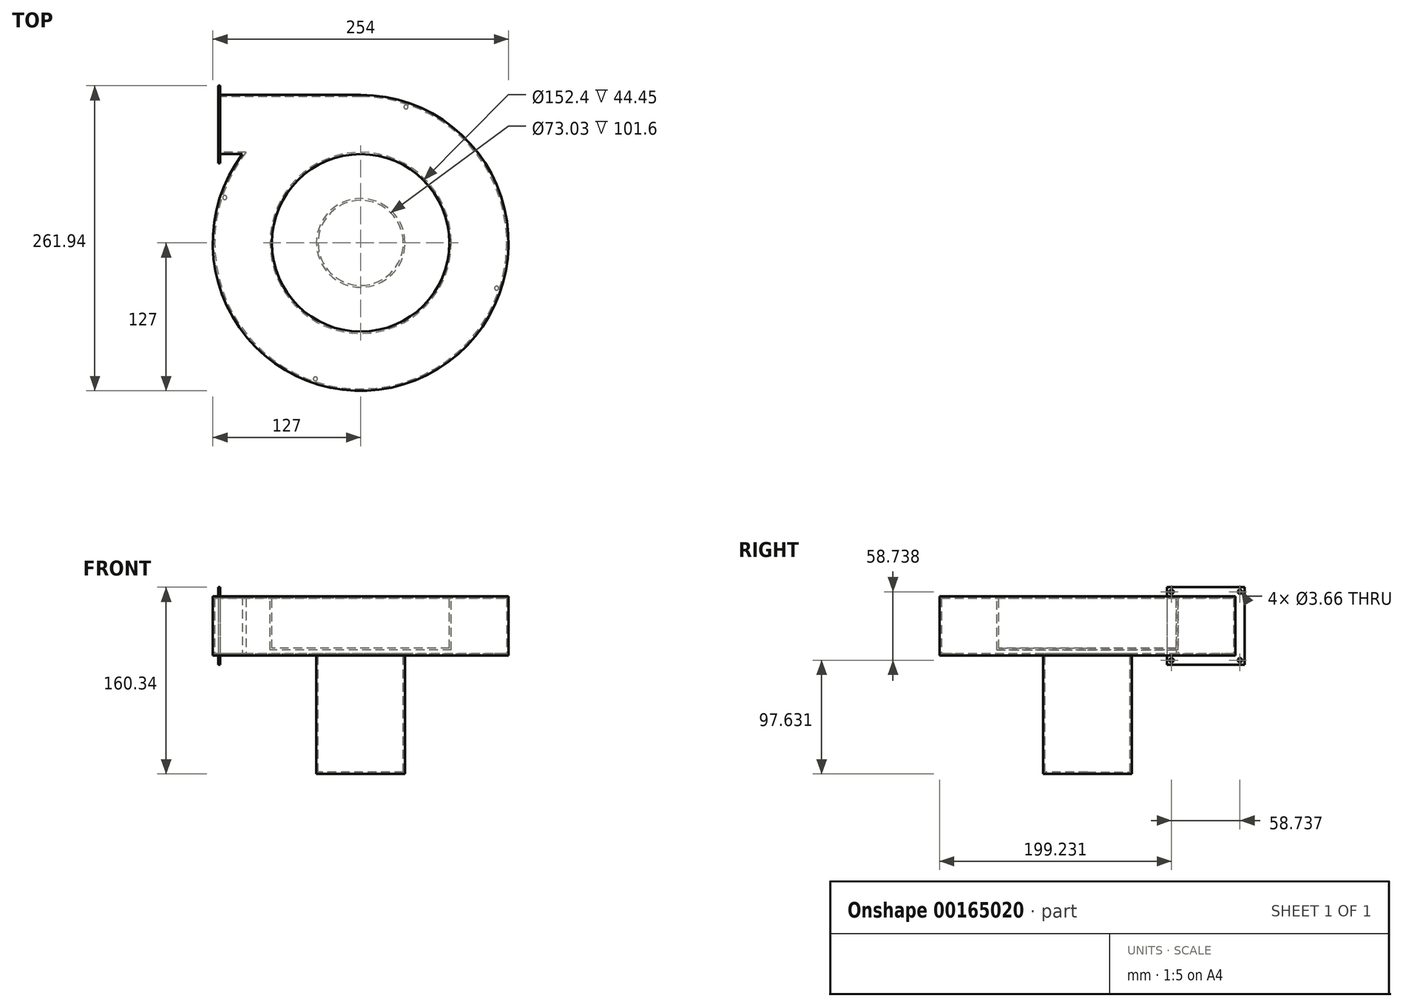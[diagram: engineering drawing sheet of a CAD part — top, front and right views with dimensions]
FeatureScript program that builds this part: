
annotation { "Feature Type Name" : "Feature", "Feature Type Description" : "" }
export const myFeature = defineFeature(function(context is Context, id is Id, definition is map)
    precondition{}
    {
        {
            var Q0;
            Q0=qCreatedBy(makeId("Top.planeOp"),FACE);
            var sketch = newSketch(context, id + "F0", { "sketchPlane" : qUnion([Q0])});
            skLineSegment(sketch, "E0.bottom", {"start": v(-101.6, 76.2) * mm, "end": v(-120.65, 76.2) * mm});
            skLineSegment(sketch, "E0.top", {"start": v(0, 127) * mm, "end": v(-120.65, 127) * mm});
            skLineSegment(sketch, "E1.top", {"start": v(-120.65, 68.26) * mm, "end": v(-122.24, 68.26) * mm});
            skLineSegment(sketch, "E1.left", {"start": v(-120.65, 76.2) * mm, "end": v(-120.65, 68.26) * mm});
            skLineSegment(sketch, "E2.top", {"start": v(-120.65, 134.94) * mm, "end": v(-122.24, 134.94) * mm});
            skLineSegment(sketch, "E2.left", {"start": v(-120.65, 127) * mm, "end": v(-120.65, 134.94) * mm});
            skLineSegment(sketch, "E3", {"start": v(-122.24, 134.94) * mm, "end": v(-122.24, 68.26) * mm});
            skLineSegment(sketch, "E4", {"start": v(-120.65, 76.2) * mm, "end": v(-120.65, 127) * mm, "construction": true});
            skArc(sketch, "E5", {"start": v(-101.6, 76.2) * mm, "mid": v(56.8, -113.6) * mm, "end": v(0, 127) * mm});
            skSolve(sketch);
        }
        {
            var Q0;
            Q0=makeQuery(id+"F0.imprint","IMPRINT",FACE,{"disambiguationData":[TD([[makeQuery(id+"F0.imprint","IMPRINT",EDGE,{"derivedFrom":sQuery(id+"F0.wireOp",EDGE,"E0.bottom")}),-1.0]])]});
            extrude(context, id + "F1", {"entities" : qUnion([Q0]), "depth" : 50.8 * mm});
        }
        {
            var Q0;
            Q0=makeQuery(id+"F1.opExtrude","CAP_FACE",FACE,{"disambiguationData":[OSD([sQuery(id+"F0.wireOp",EDGE,"E0.bottom"),sQuery(id+"F0.wireOp",EDGE,"E0.top"),sQuery(id+"F0.wireOp",EDGE,"E1.top"),sQuery(id+"F0.wireOp",EDGE,"E1.left"),sQuery(id+"F0.wireOp",EDGE,"E2.top"),sQuery(id+"F0.wireOp",EDGE,"E2.left"),sQuery(id+"F0.wireOp",EDGE,"E3"),sQuery(id+"F0.wireOp",EDGE,"E5")])],"isStart":false});
            var sketch = newSketch(context, id + "F2", { "sketchPlane" : qUnion([Q0])});
            skCircle(sketch, "E6", {"center": v(0, 0) * mm, "radius": 76.2 * mm});
            skSolve(sketch);
        }
        {
            var Q0;
            Q0 = qSketchRegion(id + "F2", true);
            extrude(context, id + "F3", {"entities" : qUnion([Q0]), "operationType" : NewBodyOperationType.REMOVE, "oppositeDirection" : true, "depth" : 44.45 * mm});
        }
        {
            var Q0;
            Q0=makeQuery(id+"F1.opExtrude","CAP_FACE",FACE,{"disambiguationData":[OSD([sQuery(id+"F0.wireOp",EDGE,"E0.bottom"),sQuery(id+"F0.wireOp",EDGE,"E0.top"),sQuery(id+"F0.wireOp",EDGE,"E1.top"),sQuery(id+"F0.wireOp",EDGE,"E1.left"),sQuery(id+"F0.wireOp",EDGE,"E2.top"),sQuery(id+"F0.wireOp",EDGE,"E2.left"),sQuery(id+"F0.wireOp",EDGE,"E3"),sQuery(id+"F0.wireOp",EDGE,"E5")])],"isStart":true});
            var sketch = newSketch(context, id + "F4", { "sketchPlane" : qUnion([Q0])});
            skCircle(sketch, "E7", {"center": v(0, 0) * mm, "radius": 38.1 * mm});
            skSolve(sketch);
        }
        {
            var Q0;
            Q0=makeQuery(id+"F4.imprint","IMPRINT",FACE,{"disambiguationData":[TD([[makeQuery(id+"F4.imprint","IMPRINT",EDGE,{"derivedFrom":sQuery(id+"F4.wireOp",EDGE,"E7")}),1.0]])]});
            extrude(context, id + "F5", {"entities" : qUnion([Q0]), "operationType" : NewBodyOperationType.ADD, "depth" : 101.6 * mm});
        }
        {
            var Q0;
            Q0=makeQuery(id+"F1.opExtrude","SWEPT_FACE",FACE,{"disambiguationData":[OSD([sQuery(id+"F0.wireOp",EDGE,"E3")])]});
            shell(context, id + "F6", {"entities" : qUnion([Q0]), "thickness" : 1.59 * mm});
        }
        {
            var Q0;
            Q0=makeQuery(id+"F1.opExtrude","SWEPT_FACE",FACE,{"disambiguationData":[OSD([sQuery(id+"F0.wireOp",EDGE,"E3")])]});
            var sketch = newSketch(context, id + "F7", { "sketchPlane" : qUnion([Q0])});
            skLineSegment(sketch, "E8.bottom", {"start": v(-125.41, 49.21) * mm, "end": v(-77.79, 49.21) * mm});
            skLineSegment(sketch, "E8.top", {"start": v(-125.41, 1.59) * mm, "end": v(-77.79, 1.59) * mm});
            skLineSegment(sketch, "E8.left", {"start": v(-125.41, 49.21) * mm, "end": v(-125.41, 1.59) * mm});
            skLineSegment(sketch, "E8.right", {"start": v(-77.79, 49.21) * mm, "end": v(-77.79, 1.59) * mm});
            skPoint(sketch, "E8.middle", {"position": v(-101.6, 25.4) * mm});
            skLineSegment(sketch, "E9.bottom", {"start": v(-68.26, 58.74) * mm, "end": v(-134.94, 58.74) * mm});
            skLineSegment(sketch, "E9.top", {"start": v(-68.26, -7.94) * mm, "end": v(-134.94, -7.94) * mm});
            skLineSegment(sketch, "E9.left", {"start": v(-68.26, 58.74) * mm, "end": v(-68.26, -7.94) * mm});
            skLineSegment(sketch, "E9.right", {"start": v(-134.94, 58.74) * mm, "end": v(-134.94, -7.94) * mm});
            skSolve(sketch);
        }
        {
            var Q0;
            Q0 = qSketchRegion(id + "F7", true);
            var Q1;
            Q1=makeQuery(id+"F1.opExtrude","SWEPT_FACE",FACE,{"disambiguationData":[OSD([sQuery(id+"F0.wireOp",EDGE,"E2.left")])]});
            extrude(context, id + "F8", {"entities" : qUnion([Q0]), "operationType" : NewBodyOperationType.ADD, "endBound" : BoundingType.UP_TO_SURFACE, "oppositeDirection" : true, "endBoundEntityFace" : qUnion([Q1]), "depth" : 25.4 * mm});
        }
        {
            var Q0;
            Q0=makeQuery(id+"F1.opExtrude","SWEPT_FACE",FACE,{"disambiguationData":[OSD([sQuery(id+"F0.wireOp",EDGE,"E3")])]});
            var sketch = newSketch(context, id + "F9", { "sketchPlane" : qUnion([Q0])});
            skLineSegment(sketch, "E10", {"start": v(-101.6, 49.21) * mm, "end": v(-101.6, 1.59) * mm, "construction": true});
            skLineSegment(sketch, "E11.bottom", {"start": v(-130.97, 58.74) * mm, "end": v(-134.94, 58.74) * mm, "construction": true});
            skLineSegment(sketch, "E11.top", {"start": v(-130.97, 54.77) * mm, "end": v(-134.94, 54.77) * mm, "construction": true});
            skLineSegment(sketch, "E11.left", {"start": v(-130.97, 58.74) * mm, "end": v(-130.97, 54.77) * mm, "construction": true});
            skLineSegment(sketch, "E11.right", {"start": v(-134.94, 58.74) * mm, "end": v(-134.94, 54.77) * mm, "construction": true});
            skLineSegment(sketch, "E12.bottom", {"start": v(-130.97, 54.77) * mm, "end": v(-72.23, 54.77) * mm, "construction": true});
            skLineSegment(sketch, "E12.top", {"start": v(-130.97, -3.97) * mm, "end": v(-72.23, -3.97) * mm, "construction": true});
            skLineSegment(sketch, "E12.left", {"start": v(-130.97, 54.77) * mm, "end": v(-130.97, -3.97) * mm, "construction": true});
            skLineSegment(sketch, "E12.right", {"start": v(-72.23, 54.77) * mm, "end": v(-72.23, -3.97) * mm, "construction": true});
            skPoint(sketch, "E12.middle", {"position": v(-101.6, 25.4) * mm});
            skCircle(sketch, "E13", {"center": v(-130.97, 54.77) * mm, "radius": 1.83 * mm});
            skCircle(sketch, "E14", {"center": v(-72.23, 54.77) * mm, "radius": 1.83 * mm});
            skCircle(sketch, "E15", {"center": v(-72.23, -3.97) * mm, "radius": 1.83 * mm});
            skCircle(sketch, "E16", {"center": v(-130.97, -3.97) * mm, "radius": 1.83 * mm});
            skSolve(sketch);
        }
        {
            var Q0;
            Q0 = qSketchRegion(id + "F9", true);
            var Q1;
            Q1=makeQuery(id+"F1.opExtrude","SWEPT_FACE",FACE,{"disambiguationData":[OSD([sQuery(id+"F0.wireOp",EDGE,"E2.left")])]});
            extrude(context, id + "F10", {"entities" : qUnion([Q0]), "operationType" : NewBodyOperationType.REMOVE, "endBound" : BoundingType.UP_TO_SURFACE, "oppositeDirection" : true, "endBoundEntityFace" : qUnion([Q1]), "depth" : 25.4 * mm});
        }
        {
            var Q0;
            Q0=makeQuery(id+"F1.opExtrude","CAP_FACE",FACE,{"disambiguationData":[OSD([sQuery(id+"F0.wireOp",EDGE,"E0.bottom"),sQuery(id+"F0.wireOp",EDGE,"E0.top"),sQuery(id+"F0.wireOp",EDGE,"E1.top"),sQuery(id+"F0.wireOp",EDGE,"E1.left"),sQuery(id+"F0.wireOp",EDGE,"E2.top"),sQuery(id+"F0.wireOp",EDGE,"E2.left"),sQuery(id+"F0.wireOp",EDGE,"E3"),sQuery(id+"F0.wireOp",EDGE,"E5")])],"isStart":true});
            var sketch = newSketch(context, id + "F11", { "sketchPlane" : qUnion([Q0])});
            skLineSegment(sketch, "E17.bottom", {"start": v(-116.72, -38.9) * mm, "end": v(-38.9, 116.72) * mm, "construction": true});
            skLineSegment(sketch, "E17.top", {"start": v(38.9, -116.72) * mm, "end": v(116.72, 38.9) * mm, "construction": true});
            skLineSegment(sketch, "E17.left", {"start": v(-116.72, -38.9) * mm, "end": v(38.9, -116.72) * mm, "construction": true});
            skLineSegment(sketch, "E17.right", {"start": v(-38.9, 116.72) * mm, "end": v(116.72, 38.9) * mm, "construction": true});
            skPoint(sketch, "E17.middle", {"position": v(0, 0) * mm});
            skCircle(sketch, "E18", {"center": v(-38.9, 116.72) * mm, "radius": 3.97 * mm, "construction": true});
            skArc(sketch, "E19", {"start": v(-101.6, -76.2) * mm, "mid": v(-56.8, -113.6) * mm, "end": v(0, -127) * mm, "construction": true});
            skLineSegment(sketch, "E20", {"start": v(0, 0) * mm, "end": v(-38.9, -77.81) * mm, "construction": true});
            skLineSegment(sketch, "E21", {"start": v(-38.9, -77.81) * mm, "end": v(-56.8, -113.6) * mm, "construction": true});
            skCircle(sketch, "E22", {"center": v(38.9, -116.72) * mm, "radius": 1.73 * mm});
            skCircle(sketch, "E23", {"center": v(-116.72, -38.9) * mm, "radius": 1.73 * mm});
            skCircle(sketch, "E24", {"center": v(-38.9, 116.72) * mm, "radius": 1.73 * mm});
            skCircle(sketch, "E25", {"center": v(116.72, 38.9) * mm, "radius": 1.73 * mm});
            skSolve(sketch);
        }
        {
            var Q0;
            Q0 = qSketchRegion(id + "F11", true);
            extrude(context, id + "F12", {"entities" : qUnion([Q0]), "operationType" : NewBodyOperationType.REMOVE, "oppositeDirection" : true, "depth" : 12.7 * mm});
        }
    });
